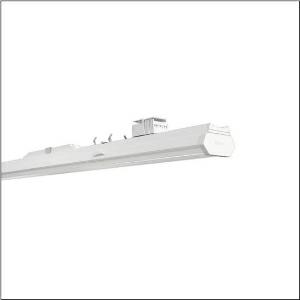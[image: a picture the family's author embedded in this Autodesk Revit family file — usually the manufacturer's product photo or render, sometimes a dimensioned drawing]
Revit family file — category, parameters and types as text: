
# Revit family: licross_r__11_protected_mo_51td1bcn485g_09c4
name_source: partatom
category: Lighting Fixtures
units: mm (PartAtom-declared; Revit-internal decimal feet)

## family parameters
Cut with Voids When Loaded = No
Host = Face
Light Source = No
Part Type = Normal
Room Calculation Point = No
Round Connector Dimension = Use Diameter
Shared = No

## types (1)
- --- (1 x LED, 8520 lm, 49.4 W, 4000K)
    Apparent Load = 49 VA
    CIE Flux Codes = 54 82 95 97 100
    Color Rendering = 80
    Color Temperature = 4000K
    Default Elevation = 1800 mm
    Description = Licross® 11 Protected MO, luminaire insert, of sheet steel, galvanised, coil coated, white, length: 1.500mm, width: 90mm, height: 101mm, LED rated luminous flux: 8.520lm, light colour: 840, control gear: ON/OFF Multilumen, CLOi, with plug, 3-pole, with phase selection, mains connection: 220..240V, AC, 50/60Hz, start of lifetime: 49W, end of service life: 55W, internal wiring halogen-free, primary optical cover: cover, of PMMA, light emission: direct distribution, primary light characteristic: symmetric, protection rating (complete): IP54, insulation class (complete): insulation class I (protective earthing), certification: CE, ENEC, VDE, UKCA, protection symbol: D if used in an environment with non-conductive dust loads with corresponding accessories, impact resistance: IK06, permissible ambient temperature for indoor applications: -35..+40°C, corresponds to IFS (International Featured Standards) requirements for safety and quality in the food industry, reducing of maximum allowable ambient temperature of 5°C with ceiling mounting, LABS conformity tested according to VDMA 24364:2018-05, packaging unit: 1 piece
    Height = 92 mm
    Lamp = 1 x LED
    Lamp Light Flux = 8520 lm
    Lamp Power = 49.4 W
    Lamp count = 1
    Length = 1500 mm
    Luminous efficacy = 172 lm/W
    Manufacturer = Siteco
    ModVariant = No
    Model = 51TD1BCN485G
    Mounting Place = Ceiling
    Mounting Type = Pendant
    Number of Poles = 1
    OnlyDefault = Yes
    Power Factor = 1
    Product Name = Licross® 11 Protected MO
    Product group = luminaire insert | ceiling pendant
    ProductGroupID = 902
    Protection Class = Protection class I
    Protection Degree = IP 54
    RLX_Detail_Level = 1
    RLX_Emergency_Light_Flux = 0 lm
    RLX_Emergency_Type = 0
    RLX_Emergency_Type_DB = No
    RlxData = <blob elided: 22153 chars, md5=c1b0bd64>
    Socket = socket
    Standby Power = 0 W
    System Light Flux = 8520 lm
    System Power = 49 W
    Type Comments = factory setting: luminous flux: 100 % | (A | C | E) | 113 mA
    Type Image = l_1256145.jpg
    URL = http://relux.com
    VarID = @adj_107521
    Voltage = 0 V
    Weight = 0.00 kg
    Width = 88 mm

## geometry (parser evidence)
native form markers: Blend x4, Sweep x13
no freeform markers — native parametric forms only
